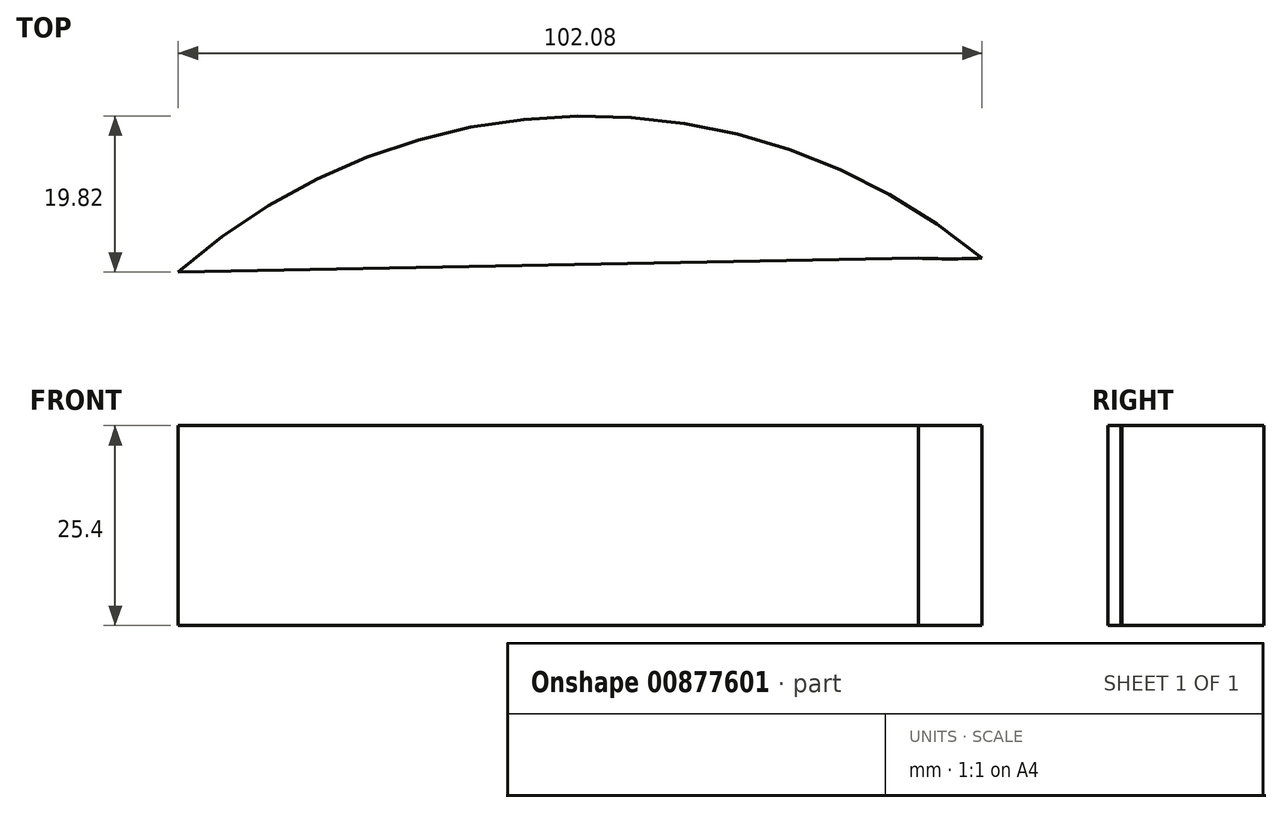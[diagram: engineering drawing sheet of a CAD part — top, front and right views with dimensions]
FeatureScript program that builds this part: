
annotation { "Feature Type Name" : "Feature", "Feature Type Description" : "" }
export const myFeature = defineFeature(function(context is Context, id is Id, definition is map)
    precondition{}
    {
        {
            var Q0;
            Q0=qCreatedBy(makeId("Top.planeOp"),FACE);
            var sketch = newSketch(context, id + "F0", { "sketchPlane" : qUnion([Q0])});
            skArc(sketch, "E0", {"start": v(0, 0) * mm, "mid": v(-51.37, 18.04) * mm, "end": v(-102.08, -1.77) * mm});
            skArc(sketch, "E1", {"start": v(-8.08, 0) * mm, "mid": v(-4.04, -0.1) * mm, "end": v(0, 0) * mm});
            skLineSegment(sketch, "E2", {"start": v(-102.08, -1.77) * mm, "end": v(-8.08, 0) * mm});
            skSolve(sketch);
        }
        {
            var Q0;
            Q0 = qSketchRegion(id + "F0", true);
            extrude(context, id + "F1", {"entities" : qUnion([Q0]), "depth" : 25.4 * mm, "offsetDistance" : 25.4 * mm});
        }
    });
